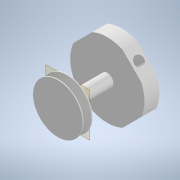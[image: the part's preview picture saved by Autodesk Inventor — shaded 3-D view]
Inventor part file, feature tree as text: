
AUTODESK INVENTOR PART (.ipt)
format: ipt  version: 2021 (Build 250183000, 183)  size: 171,008 bytes
history: native  units: mm
features: extrude x7, sketch x7, other x4, chamfer x2, reference x1, projected_geometry x1
ambient origin geometry x8: Origin, YZ Plane, XZ Plane, XY Plane, X Axis, Y Axis, Z Axis, Center Point
bodies: Body1 (feature_tree)
feature tree (22):
  other  "Bryła1"
  other  "Płaszczyzna konstrukcyjna1"
  extrude  "Wyciągnięcie proste1"  Depth=25.0mm
  extrude  "Wyciągnięcie proste2"  Depth=20.0mm TaperAngle=0.0deg
  chamfer  "Faza1"  Distance=100.0mm
  extrude  "Wyciągnięcie proste3"  Depth=10.0mm TaperAngle=0.0deg
  chamfer  "Faza2"  Distance=37.0mm Angle=45.0deg
  extrude  "Wyciągnięcie proste4"  Depth=100.0mm
  extrude  "Wyciągnięcie proste5"  Depth=10.0mm TaperAngle=0.0deg
  extrude  "Wyciągnięcie proste6"  Depth=37.0mm TaperAngle=45.0deg
  extrude  "Wyciągnięcie proste7"  Depth=150.0mm
  sketch  "Szkic1"
  reference  "Odniesienie1"
  sketch  "Szkic2"
  sketch  "Szkic3"
  sketch  "Szkic4"
  sketch  "Szkic5"
  sketch  "Szkic6"
  sketch  "Szkic7"
  projected_geometry  "Pętla rzutowana1"
  other  "Zespół1"
  other  "jakis_modulxD:1"
